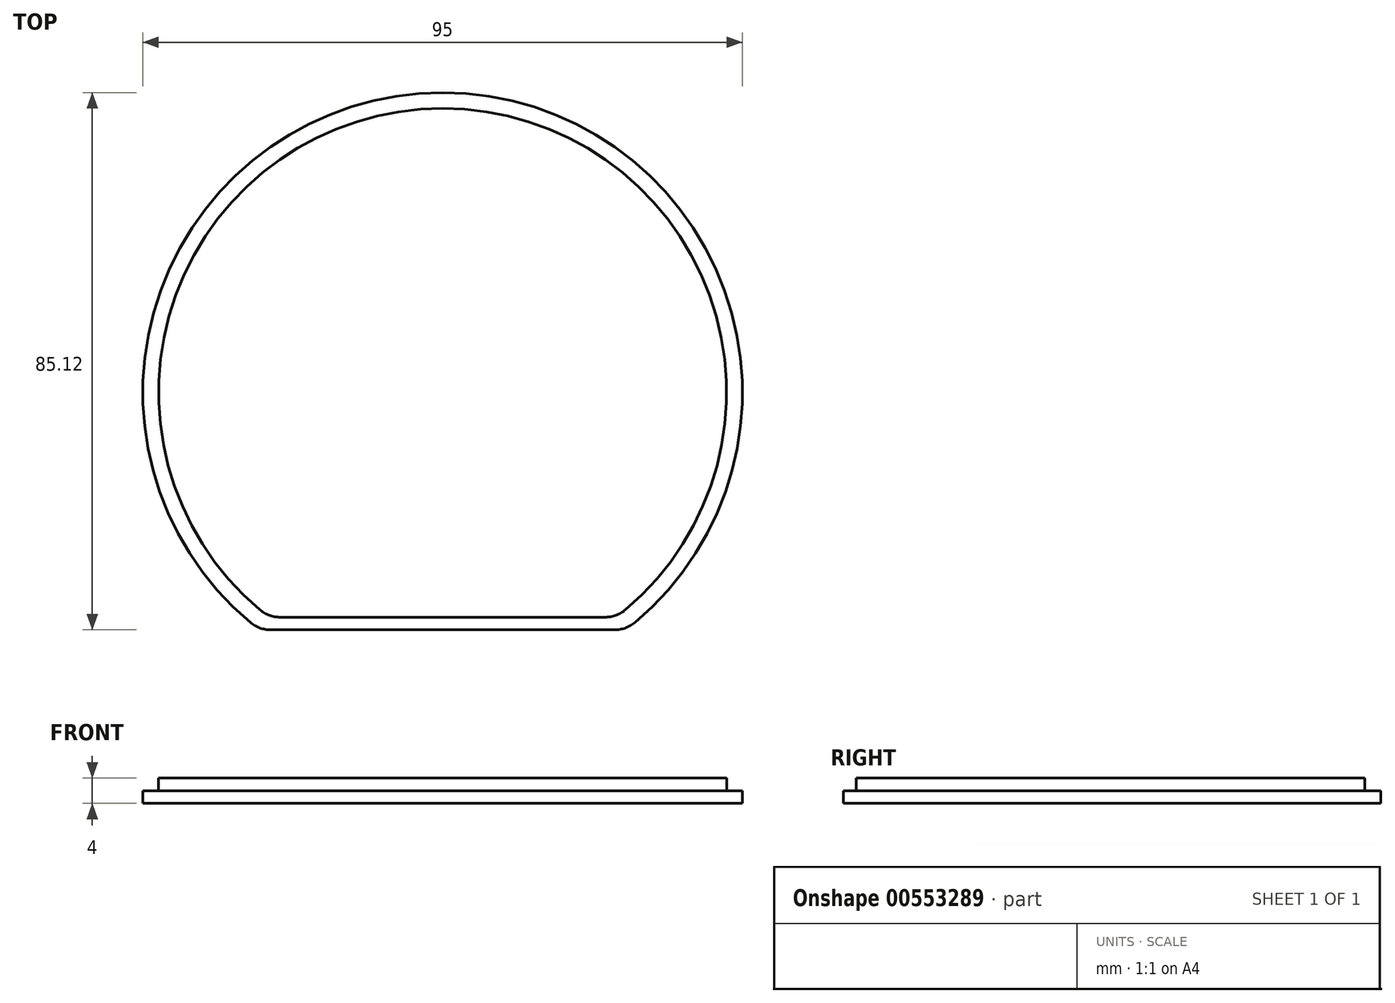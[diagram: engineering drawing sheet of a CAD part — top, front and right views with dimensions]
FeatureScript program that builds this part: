
annotation { "Feature Type Name" : "Feature", "Feature Type Description" : "" }
export const myFeature = defineFeature(function(context is Context, id is Id, definition is map)
    precondition{}
    {
        {
            var Q0;
            Q0=qCreatedBy(makeId("Top.planeOp"),FACE);
            var sketch = newSketch(context, id + "F0", { "sketchPlane" : qUnion([Q0])});
            skArc(sketch, "E0", {"start": v(27.5, -35.62) * mm, "mid": v(0, 45) * mm, "end": v(-27.5, -35.62) * mm});
            skLineSegment(sketch, "E1", {"start": v(-27.5, -35.62) * mm, "end": v(27.5, -35.62) * mm});
            skSolve(sketch);
        }
        {
            var Q0;
            Q0=makeQuery(id+"F0.imprint","IMPRINT",FACE,{"disambiguationData":[TD([[makeQuery(id+"F0.imprint","IMPRINT",EDGE,{"derivedFrom":sQuery(id+"F0.wireOp",EDGE,"E0")}),1.0]])]});
            extrude(context, id + "F1", {"entities" : qUnion([Q0]), "depth" : 2 * mm, "offsetDistance" : 25 * mm});
        }
        {
            var Q0;
            Q0=makeQuery(id+"F1.opExtrude","CAP_FACE",FACE,{"disambiguationData":[OSD([sQuery(id+"F0.wireOp",EDGE,"E0"),sQuery(id+"F0.wireOp",EDGE,"E1")])],"isStart":true});
            var sketch = newSketch(context, id + "F2", { "sketchPlane" : qUnion([Q0])});
            skArc(sketch, "E2", {"start": v(-29, 37.62) * mm, "mid": v(0, -47.5) * mm, "end": v(29, 37.62) * mm});
            skLineSegment(sketch, "E3", {"start": v(29, 37.62) * mm, "end": v(-29, 37.62) * mm});
            skSolve(sketch);
        }
        {
            var Q0;
            Q0=makeQuery(id+"F2.imprint","IMPRINT",FACE,{"disambiguationData":[TD([[makeQuery(id+"F2.imprint","IMPRINT",EDGE,{"derivedFrom":sQuery(id+"F2.wireOp",EDGE,"E2")}),1.0]])]});
            var Q1;
            Q1=makeQuery(id+"F2.imprint","IMPRINT",FACE,{"disambiguationData":[TD([[makeQuery(id+"F2.imprint","IMPRINT",EDGE,{"derivedFrom":makeQuery(id+"F1.opExtrude","CAP_EDGE",EDGE,{"disambiguationData":[OSD([sQuery(id+"F0.wireOp",EDGE,"E0")])],"isStart":true})}),-1.0]])]});
            extrude(context, id + "F3", {"entities" : qUnion([Q0, Q1]), "operationType" : NewBodyOperationType.ADD, "depth" : 2 * mm, "offsetDistance" : 25 * mm});
        }
        {
            var Q0;
            {var subQ0=sQuery(id+"F0.wireOp",EDGE,"E1");var subQ1=sQuery(id+"F0.wireOp",EDGE,"E0");Q0=makeQuery(id+"F1.opExtrude","SWEPT_EDGE",EDGE,{"disambiguationData":[OSD([subQ1,subQ0]),TDD([makeQuery(id+"F0.imprint","INTERSECT",VERTEX,{"disambiguationData":[OD(0.0)],"derivedFrom":[subQ1,subQ0]})])]});}
            var Q1;
            {var subQ0=sQuery(id+"F0.wireOp",EDGE,"E1");var subQ1=sQuery(id+"F0.wireOp",EDGE,"E0");Q1=makeQuery(id+"F1.opExtrude","SWEPT_EDGE",EDGE,{"disambiguationData":[OSD([subQ1,subQ0]),TDD([makeQuery(id+"F0.imprint","INTERSECT",VERTEX,{"disambiguationData":[OD(1.0)],"derivedFrom":[subQ1,subQ0]})])]});}
            var Q2;
            {var subQ0=sQuery(id+"F2.wireOp",EDGE,"E3");var subQ1=sQuery(id+"F2.wireOp",EDGE,"E2");Q2=makeQuery(id+"F3.opExtrude","SWEPT_EDGE",EDGE,{"disambiguationData":[OSD([subQ1,subQ0]),TDD([makeQuery(id+"F2.imprint","INTERSECT",VERTEX,{"disambiguationData":[OD(0.0)],"derivedFrom":[subQ1,subQ0]})])]});}
            var Q3;
            {var subQ0=sQuery(id+"F2.wireOp",EDGE,"E3");var subQ1=sQuery(id+"F2.wireOp",EDGE,"E2");Q3=makeQuery(id+"F3.opExtrude","SWEPT_EDGE",EDGE,{"disambiguationData":[OSD([subQ1,subQ0]),TDD([makeQuery(id+"F2.imprint","INTERSECT",VERTEX,{"disambiguationData":[OD(1.0)],"derivedFrom":[subQ1,subQ0]})])]});}
            fillet(context, id + "F4", {"entities" : qUnion([Q0, Q1, Q2, Q3]), "radius" : 5 * mm, "tangentPropagation" : true, "allowEdgeOverflow" : false});
        }
    });
